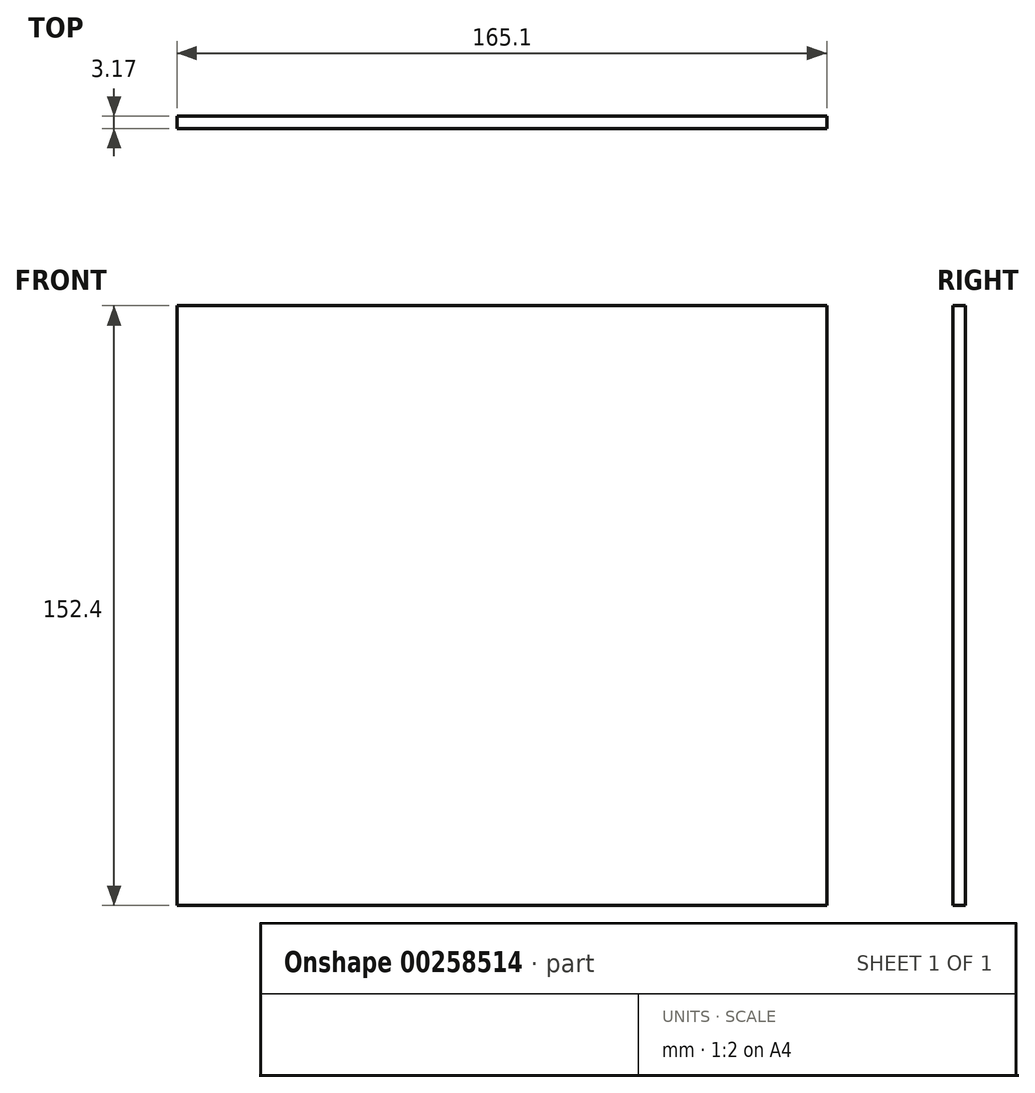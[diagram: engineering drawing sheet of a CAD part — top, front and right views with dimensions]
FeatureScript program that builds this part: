
annotation { "Feature Type Name" : "Feature", "Feature Type Description" : "" }
export const myFeature = defineFeature(function(context is Context, id is Id, definition is map)
    precondition{}
    {
        {
            var Q0;
            Q0=qCreatedBy(makeId("Front.planeOp"),FACE);
            var sketch = newSketch(context, id + "F0", { "sketchPlane" : qUnion([Q0])});
            skLineSegment(sketch, "E0.bottom", {"start": v(82.55, 76.2) * mm, "end": v(-82.55, 76.2) * mm});
            skLineSegment(sketch, "E0.top", {"start": v(82.55, -76.2) * mm, "end": v(-82.55, -76.2) * mm});
            skLineSegment(sketch, "E0.left", {"start": v(82.55, 76.2) * mm, "end": v(82.55, -76.2) * mm});
            skLineSegment(sketch, "E0.right", {"start": v(-82.55, 76.2) * mm, "end": v(-82.55, -76.2) * mm});
            skPoint(sketch, "E0.middle", {"position": v(0, 0) * mm});
            skSolve(sketch);
        }
        {
            var Q0;
            Q0 = qSketchRegion(id + "F0", true);
            extrude(context, id + "F1", {"entities" : qUnion([Q0]), "depth" : 3.17 * mm});
        }
    });
